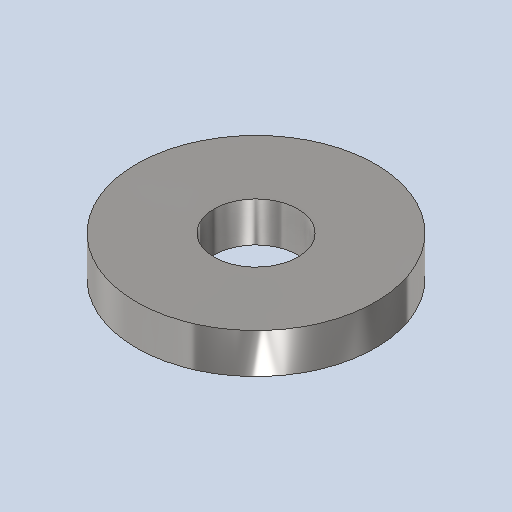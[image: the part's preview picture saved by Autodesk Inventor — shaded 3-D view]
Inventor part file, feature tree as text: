
AUTODESK INVENTOR PART (.ipt)
format: ipt  version: 2024.2 (Build 282272000, 272)  size: 242,688 bytes
history: native  units: mm
features: revolve x1, sketch x1
ambient origin geometry x8: Origin, YZ Plane, XZ Plane, XY Plane, X Axis, Y Axis, Z Axis, Center Point
bodies: Solid1 (feature_tree)
feature tree (2):
  revolve  "Revolution1"  [1 undecoded]
  sketch  "Sketch1"  dims[d5=90.0deg]
note: 1 required parameter value undecoded (feature->parameter linkage not recoverable at this tier; creation-order binding heuristic only, values carry confidence <= 0.55)
